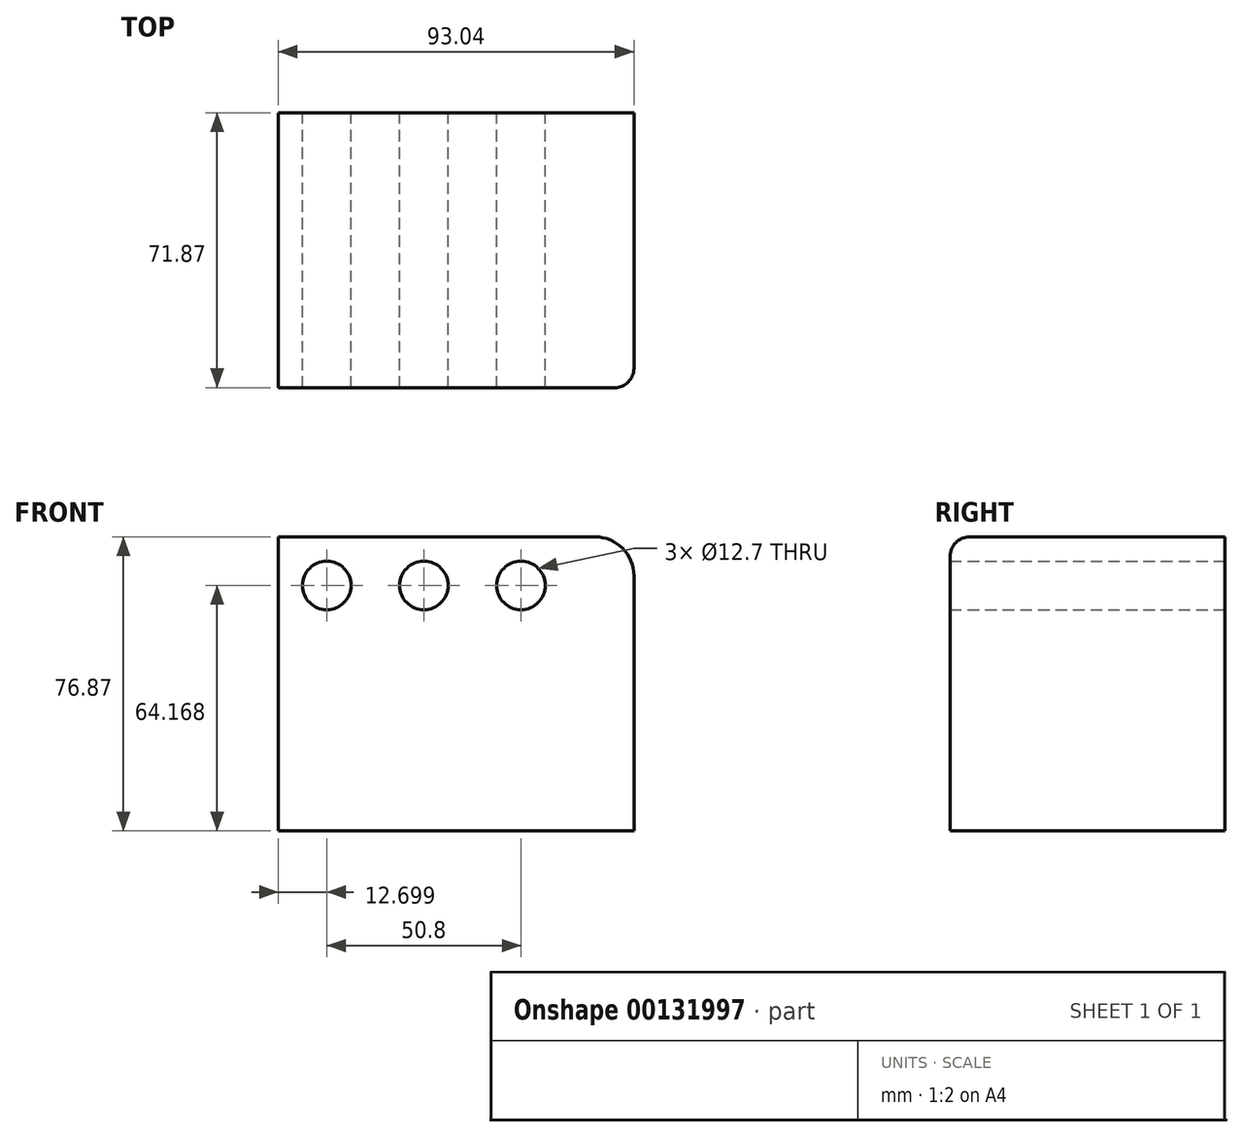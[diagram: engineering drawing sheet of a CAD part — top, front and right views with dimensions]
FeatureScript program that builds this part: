
annotation { "Feature Type Name" : "Feature", "Feature Type Description" : "" }
export const myFeature = defineFeature(function(context is Context, id is Id, definition is map)
    precondition{}
    {
        {
            var Q0;
            Q0=qCreatedBy(makeId("Front.planeOp"),FACE);
            var sketch = newSketch(context, id + "F0", { "sketchPlane" : qUnion([Q0])});
            skLineSegment(sketch, "E0.bottom", {"start": v(-42.81, 36.82) * mm, "end": v(50.23, 36.82) * mm});
            skLineSegment(sketch, "E0.top", {"start": v(-42.81, -40.05) * mm, "end": v(50.23, -40.05) * mm});
            skLineSegment(sketch, "E0.left", {"start": v(-42.81, 36.82) * mm, "end": v(-42.81, -40.05) * mm});
            skLineSegment(sketch, "E0.right", {"start": v(50.23, 36.82) * mm, "end": v(50.23, -40.05) * mm});
            skCircle(sketch, "E1", {"center": v(-30.11, 24.12) * mm, "radius": 6.35 * mm});
            skCircle(sketch, "E2.1.0.0", {"center": v(-4.71, 24.12) * mm, "radius": 6.35 * mm});
            skCircle(sketch, "E2.2.0.0", {"center": v(20.69, 24.12) * mm, "radius": 6.35 * mm});
            skLineSegment(sketch, "E2.direction1", {"start": v(-30.11, 24.12) * mm, "end": v(-4.71, 24.12) * mm, "construction": true});
            skSolve(sketch);
        }
        {
            var Q0;
            Q0 = qSketchRegion(id + "F0", true);
            extrude(context, id + "F1", {"entities" : qUnion([Q0]), "depth" : 71.87 * mm});
        }
        {
            var Q0;
            Q0=makeQuery(id+"F1.opExtrude","SWEPT_EDGE",EDGE,{"disambiguationData":[OSD([sQuery(id+"F0.wireOp",EDGE,"E0.bottom"),sQuery(id+"F0.wireOp",EDGE,"E0.right")])]});
            fillet(context, id + "F2", {"entities" : qUnion([Q0]), "radius" : 10.16 * mm, "tangentPropagation" : true, "allowEdgeOverflow" : false});
        }
        {
            var Q0;
            Q0=makeQuery(id+"F1.opExtrude","CAP_EDGE",EDGE,{"disambiguationData":[OSD([sQuery(id+"F0.wireOp",EDGE,"E0.bottom")])],"isStart":false});
            fillet(context, id + "F3", {"entities" : qUnion([Q0]), "radius" : 5.08 * mm, "tangentPropagation" : true, "allowEdgeOverflow" : false});
        }
    });
